# Revit family: PRE060005-FR
name_source: partatom
category: Mobilier
revit_build: Autodesk Revit 2017 (Build: 20160225_1515(x64)
units: mm (PartAtom-declared; Revit-internal decimal feet)

## family parameters
Basée sur le plan de construction = Non
Couper avec des vides une fois chargée = Non
Partagée = Non
Point de calcul de pièce = Non
Toujours verticalement = Oui

## types (1)
- 71900 Presto Miroir Inox avec Trous de Fixation - 500x400mm
    Adresse = 7, RUE RACINE - 92542 MONTROUGE CEDEX FRANCE
    Description = Miroir inox  500x400mm Classe 8 super brillant avec trous de fixation
Inox 304, Épaisseur 1 mm, Finition poli miroir
    Fabricant = LES ROBINETS PRESTO S.A.
    Finition = Inox AISI 304 (ISO Z7 CN 18.09)
    Fonction = Miroir inox Classe 8 super Brillant avec trous de fixation - Angles arrondis
Matériaux: Inox AISI 304, epaisseur 1 mm avec finition poli miroir
Dimensions: hauteur 500mm (B), largeur 400mm (A) avec trous de fixation de 6,1mm (pour vis de 6mm)
    Garantie = 2
    Hauteur = 500 mm  [stored 1.64042 ft]
    Largeur = 400 mm  [stored 1.31234 ft]
    Lien CCTP = http://www.prestodatashare.com
    Lien fiche produit = http://www.prestodatashare.com
    Lien notice d'utilisation = http://www.prestodatashare.com
    Matériau = Inox
    Modèle = 71900 Presto Miroir Inox avec Trous de Fixation - 500x400mm
    Polantis code = PRE060005
    Profondeur = 1 mm  [stored 0.00328084 ft]
    Reference = 71900
    URL = http://www.prestodatashare.com
    URL Fabricant = http://www.prestodatashare.com
    Variantes = 71900

note: [stored X ft] marks values corroborated as IEEE doubles in the binary element streams (Revit-internal decimal feet)
